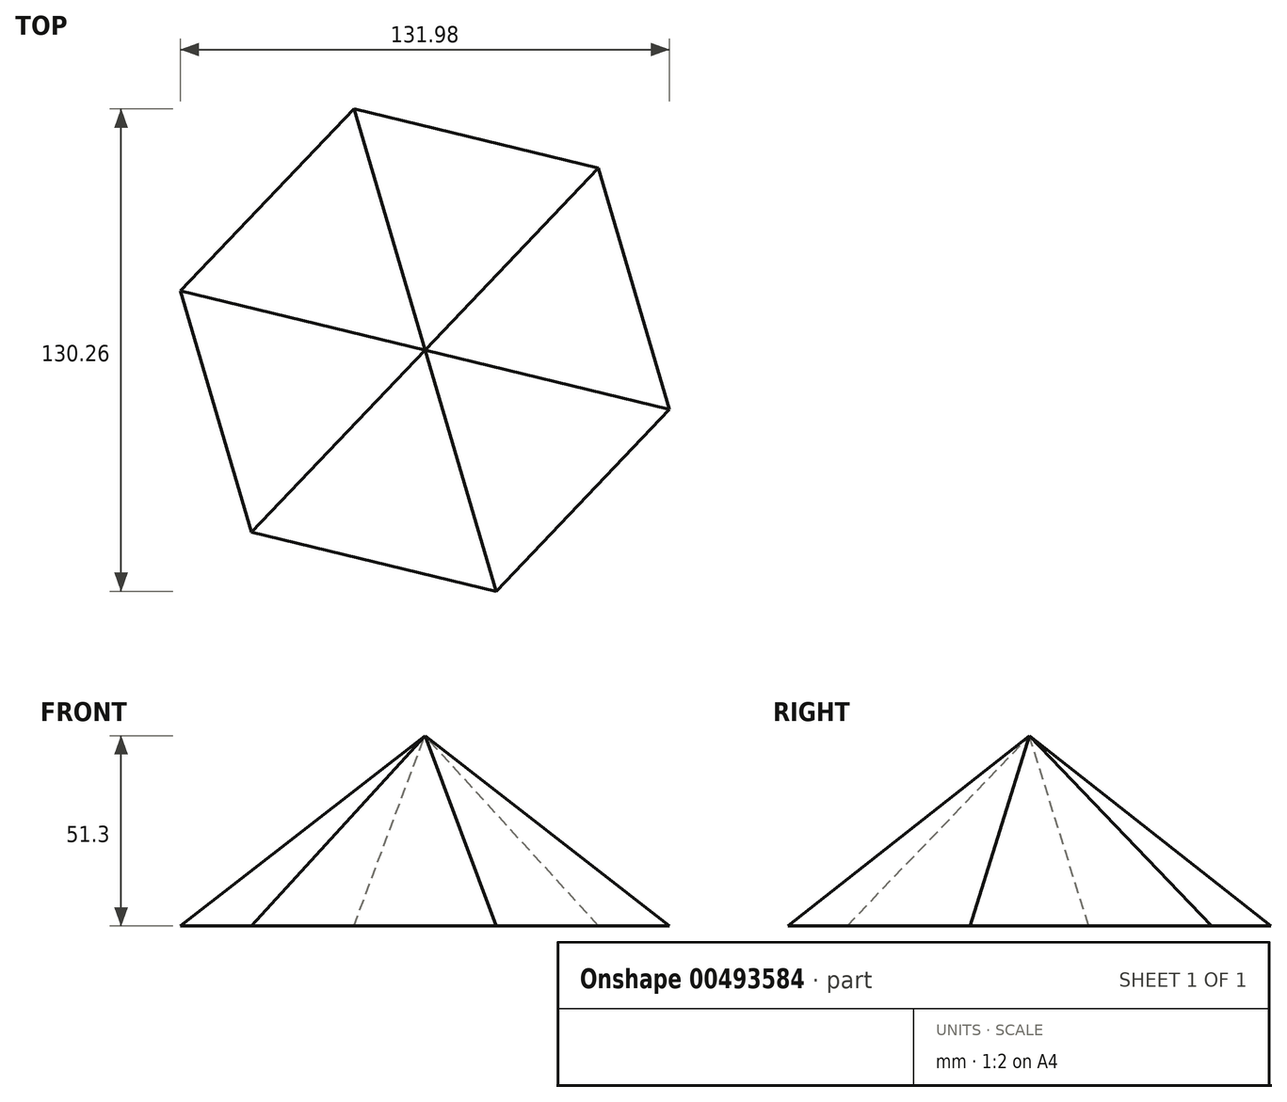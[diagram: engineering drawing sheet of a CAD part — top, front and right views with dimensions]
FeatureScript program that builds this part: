
annotation { "Feature Type Name" : "Feature", "Feature Type Description" : "" }
export const myFeature = defineFeature(function(context is Context, id is Id, definition is map)
    precondition{}
    {
        {
            var Q0;
            Q0=qCreatedBy(makeId("Top.planeOp"),FACE);
            var sketch = newSketch(context, id + "F0", { "sketchPlane" : qUnion([Q0])});
            skCircle(sketch, "E0.cCircle", {"center": v(0, 0) * mm, "radius": 67.9 * mm, "construction": true});
            skLineSegment(sketch, "E0.0", {"start": v(-46.81, -49.17) * mm, "end": v(-66, 15.96) * mm});
            skLineSegment(sketch, "E0.1", {"start": v(-66, 15.96) * mm, "end": v(-19.18, 65.13) * mm});
            skLineSegment(sketch, "E0.2", {"start": v(-19.18, 65.13) * mm, "end": v(46.81, 49.17) * mm});
            skLineSegment(sketch, "E0.3", {"start": v(46.81, 49.17) * mm, "end": v(66, -15.96) * mm});
            skLineSegment(sketch, "E0.4", {"start": v(66, -15.96) * mm, "end": v(19.18, -65.13) * mm});
            skLineSegment(sketch, "E0.5", {"start": v(19.18, -65.13) * mm, "end": v(-46.81, -49.17) * mm});
            skSolve(sketch);
        }
        {
            var Q0;
            Q0=qCreatedBy(makeId("Top.planeOp"),FACE);
            cPlane(context, id + "F1", {"entities" : qUnion([Q0]), "cplaneType" : CPlaneType.OFFSET, "offset" : 51.3 * mm, "width" : 150 * mm, "height" : 150 * mm});
        }
        {
            var Q0;
            Q0=qCreatedBy(id+"F1.planeOp",FACE);
            var sketch = newSketch(context, id + "F2", { "sketchPlane" : qUnion([Q0])});
            skPoint(sketch, "E1", {"position": v(0, 0) * mm});
            skSolve(sketch);
        }
        {
            var Q0;
            Q0=makeQuery(id+"F0.imprint","IMPRINT",FACE,{"disambiguationData":[TD([[makeQuery(id+"F0.imprint","IMPRINT",EDGE,{"derivedFrom":sQuery(id+"F0.wireOp",EDGE,"E0.0")}),-1.0]])]});
            var Q1;
            Q1=sQuery(id+"F2.wireOp",VERTEX,"E1");
            loft(context, id + "F3", {"sheetProfilesArray" : [{ "sheetProfileEntities" : qUnion([Q0]) }, { "sheetProfileEntities" : qUnion([Q1]) }]});
        }
    });
